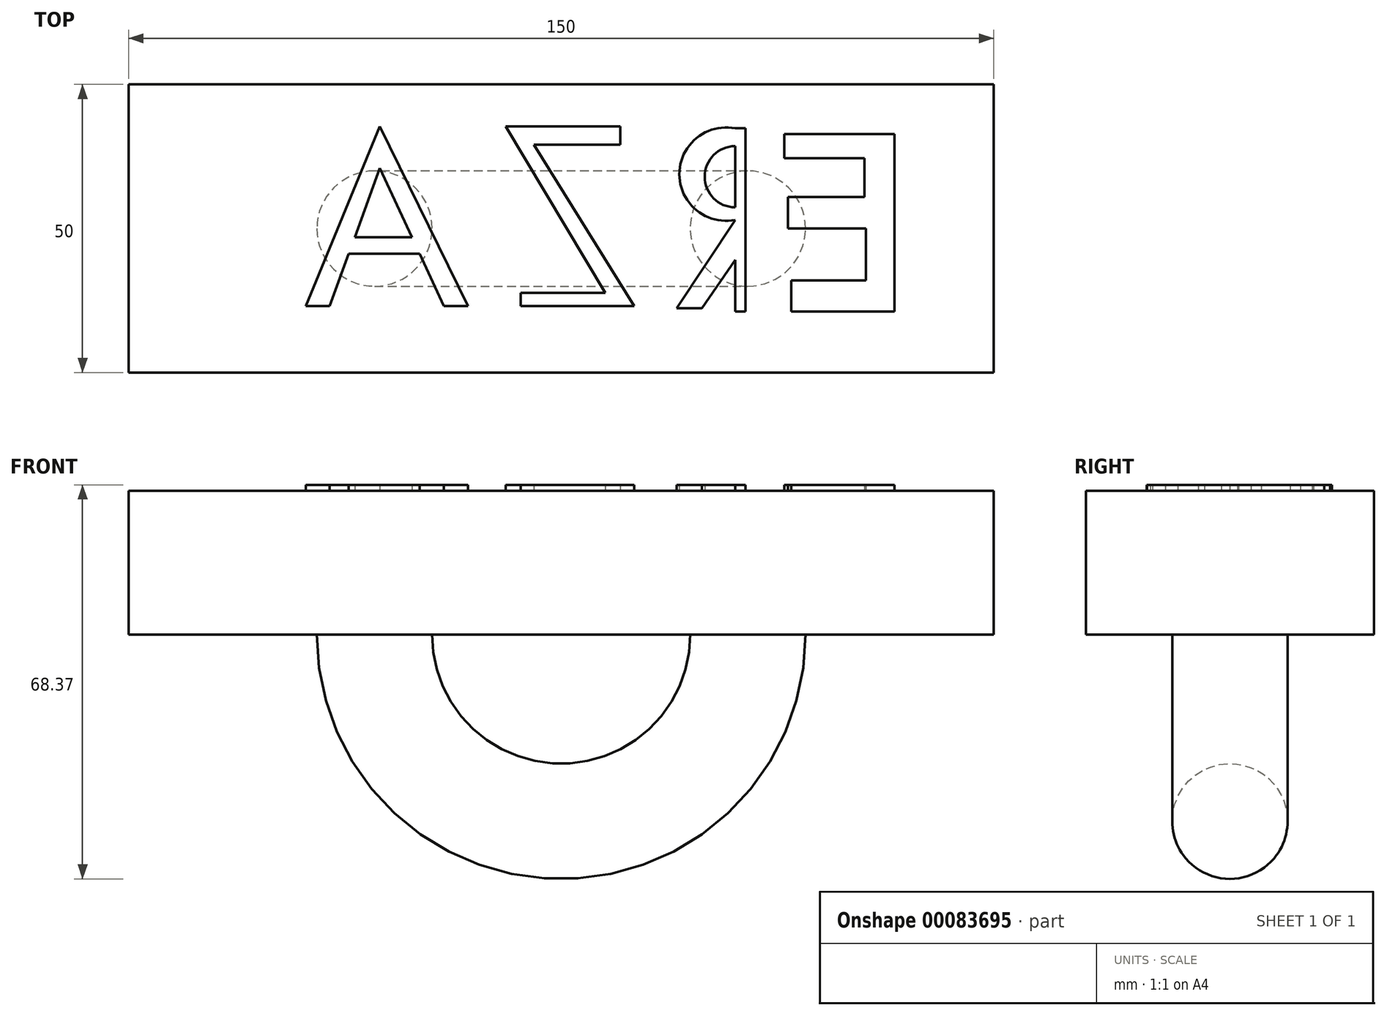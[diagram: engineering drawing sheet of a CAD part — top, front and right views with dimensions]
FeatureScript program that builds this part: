
annotation { "Feature Type Name" : "Feature", "Feature Type Description" : "" }
export const myFeature = defineFeature(function(context is Context, id is Id, definition is map)
    precondition{}
    {
        {
            var Q0;
            Q0=qCreatedBy(makeId("Top.planeOp"),FACE);
            var sketch = newSketch(context, id + "F0", { "sketchPlane" : qUnion([Q0])});
            skLineSegment(sketch, "E0.bottom", {"start": v(-75, 25) * mm, "end": v(75, 25) * mm});
            skLineSegment(sketch, "E0.top", {"start": v(-75, -25) * mm, "end": v(75, -25) * mm});
            skLineSegment(sketch, "E0.left", {"start": v(-75, 25) * mm, "end": v(-75, -25) * mm});
            skLineSegment(sketch, "E0.right", {"start": v(75, 25) * mm, "end": v(75, -25) * mm});
            skPoint(sketch, "E0.middle", {"position": v(0, 0) * mm});
            skSolve(sketch);
        }
        {
            var Q0;
            Q0=makeQuery(id+"F0.imprint","IMPRINT",FACE,{"disambiguationData":[TD([[makeQuery(id+"F0.imprint","IMPRINT",EDGE,{"derivedFrom":sQuery(id+"F0.wireOp",EDGE,"E0.bottom")}),-1.0]])]});
            extrude(context, id + "F1", {"entities" : qUnion([Q0]), "depth" : 25 * mm});
        }
        {
            var Q0;
            Q0=makeQuery(id+"F1.opExtrude","CAP_FACE",FACE,{"disambiguationData":[OSD([sQuery(id+"F0.wireOp",EDGE,"E0.bottom"),sQuery(id+"F0.wireOp",EDGE,"E0.top"),sQuery(id+"F0.wireOp",EDGE,"E0.left"),sQuery(id+"F0.wireOp",EDGE,"E0.right")])],"isStart":false});
            var sketch = newSketch(context, id + "F2", { "sketchPlane" : qUnion([Q0])});
            skLineSegment(sketch, "E1", {"start": v(38.73, 16.39) * mm, "end": v(57.8, 16.39) * mm});
            skLineSegment(sketch, "E2", {"start": v(57.8, 16.39) * mm, "end": v(57.8, -14.4) * mm});
            skLineSegment(sketch, "E3", {"start": v(57.8, -14.4) * mm, "end": v(39.92, -14.4) * mm});
            skLineSegment(sketch, "E4", {"start": v(39.92, -14.4) * mm, "end": v(39.92, -9.04) * mm});
            skLineSegment(sketch, "E5", {"start": v(39.92, -9.04) * mm, "end": v(52.83, -9.04) * mm});
            skLineSegment(sketch, "E6", {"start": v(52.83, -9.04) * mm, "end": v(52.83, 0) * mm});
            skLineSegment(sketch, "E7", {"start": v(52.83, 0) * mm, "end": v(39.33, 0) * mm});
            skLineSegment(sketch, "E8", {"start": v(39.33, 0) * mm, "end": v(39.33, 5.46) * mm});
            skLineSegment(sketch, "E9", {"start": v(39.33, 5.46) * mm, "end": v(52.63, 5.46) * mm});
            skLineSegment(sketch, "E10", {"start": v(52.63, 5.46) * mm, "end": v(52.63, 12.21) * mm});
            skLineSegment(sketch, "E11", {"start": v(52.63, 12.21) * mm, "end": v(38.73, 12.21) * mm});
            skLineSegment(sketch, "E12", {"start": v(38.73, 12.21) * mm, "end": v(38.73, 16.39) * mm});
            skLineSegment(sketch, "E13", {"start": v(30.19, -14.4) * mm, "end": v(30.19, -5.46) * mm});
            skArc(sketch, "E14", {"start": v(30.19, 17.38) * mm, "mid": v(20.5, 9.43) * mm, "end": v(30.19, 1.49) * mm});
            skLineSegment(sketch, "E15", {"start": v(30.19, 1.49) * mm, "end": v(20.06, -13.8) * mm});
            skLineSegment(sketch, "E16", {"start": v(20.06, -13.8) * mm, "end": v(24.43, -13.8) * mm});
            skLineSegment(sketch, "E17", {"start": v(24.43, -13.8) * mm, "end": v(30.19, -5.46) * mm});
            skArc(sketch, "E18", {"start": v(30.19, 14.3) * mm, "mid": v(24.9, 8.99) * mm, "end": v(30.19, 3.67) * mm});
            skPoint(sketch, "E18.startSnap0", {"position": v(38.73, 14.3) * mm});
            skLineSegment(sketch, "E19", {"start": v(30.19, 17.38) * mm, "end": v(31.97, 17.38) * mm});
            skLineSegment(sketch, "E20", {"start": v(31.97, 17.38) * mm, "end": v(31.97, -14.42) * mm});
            skLineSegment(sketch, "E21", {"start": v(31.97, -14.42) * mm, "end": v(30.19, -14.4) * mm});
            skLineSegment(sketch, "E22.trimOffspring", {"start": v(30.19, 3.67) * mm, "end": v(30.19, 14.3) * mm});
            skLineSegment(sketch, "E23", {"start": v(10.24, 17.7) * mm, "end": v(-6.72, 17.7) * mm});
            skLineSegment(sketch, "E24", {"start": v(-4.74, 14.53) * mm, "end": v(12.66, -13.44) * mm});
            skLineSegment(sketch, "E25", {"start": v(12.66, -13.44) * mm, "end": v(-7.05, -13.44) * mm});
            skLineSegment(sketch, "E26", {"start": v(10.24, 17.7) * mm, "end": v(10.24, 14.53) * mm});
            skLineSegment(sketch, "E27", {"start": v(10.24, 14.53) * mm, "end": v(-4.74, 14.53) * mm});
            skLineSegment(sketch, "E28", {"start": v(-7.05, -13.44) * mm, "end": v(-7.05, -11.19) * mm});
            skLineSegment(sketch, "E29", {"start": v(-7.05, -11.19) * mm, "end": v(7.65, -11.19) * mm});
            skLineSegment(sketch, "E30", {"start": v(7.65, -11.19) * mm, "end": v(-9.64, 17.7) * mm});
            skLineSegment(sketch, "E31", {"start": v(-9.64, 17.7) * mm, "end": v(-6.72, 17.7) * mm});
            skLineSegment(sketch, "E32", {"start": v(-16.18, -13.44) * mm, "end": v(-31.46, 17.73) * mm});
            skLineSegment(sketch, "E33", {"start": v(-31.46, 17.73) * mm, "end": v(-44.32, -13.44) * mm});
            skLineSegment(sketch, "E34", {"start": v(-44.32, -13.44) * mm, "end": v(-40.14, -13.44) * mm});
            skLineSegment(sketch, "E35", {"start": v(-40.14, -13.44) * mm, "end": v(-36.85, -4.38) * mm});
            skLineSegment(sketch, "E36", {"start": v(-31.46, 10.46) * mm, "end": v(-25.9, -1.49) * mm});
            skLineSegment(sketch, "E37", {"start": v(-20.35, -13.44) * mm, "end": v(-16.18, -13.44) * mm});
            skLineSegment(sketch, "E38", {"start": v(-25.9, -1.49) * mm, "end": v(-35.8, -1.49) * mm});
            skLineSegment(sketch, "E39", {"start": v(-36.85, -4.38) * mm, "end": v(-24.56, -4.38) * mm});
            skLineSegment(sketch, "E40.trimOffspring", {"start": v(-24.56, -4.38) * mm, "end": v(-20.35, -13.44) * mm});
            skLineSegment(sketch, "E41.trimOffspring", {"start": v(-35.8, -1.49) * mm, "end": v(-31.46, 10.46) * mm});
            skSolve(sketch);
        }
        {
            var Q0;
            Q0=makeQuery(id+"F2.imprint","IMPRINT",FACE,{"disambiguationData":[TD([[makeQuery(id+"F2.imprint","IMPRINT",EDGE,{"derivedFrom":sQuery(id+"F2.wireOp",EDGE,"E32")}),1.0]])]});
            var Q1;
            Q1=makeQuery(id+"F2.imprint","IMPRINT",FACE,{"disambiguationData":[TD([[makeQuery(id+"F2.imprint","IMPRINT",EDGE,{"derivedFrom":sQuery(id+"F2.wireOp",EDGE,"E23")}),1.0]])]});
            var Q2;
            Q2=makeQuery(id+"F2.imprint","IMPRINT",FACE,{"disambiguationData":[TD([[makeQuery(id+"F2.imprint","IMPRINT",EDGE,{"derivedFrom":sQuery(id+"F2.wireOp",EDGE,"E13")}),-1.0]])]});
            var Q3;
            Q3=makeQuery(id+"F2.imprint","IMPRINT",FACE,{"disambiguationData":[TD([[makeQuery(id+"F2.imprint","IMPRINT",EDGE,{"derivedFrom":sQuery(id+"F2.wireOp",EDGE,"E1")}),-1.0]])]});
            extrude(context, id + "F3", {"entities" : qUnion([Q0, Q1, Q2, Q3]), "operationType" : NewBodyOperationType.ADD, "depth" : 1 * mm});
        }
        {
            var Q0;
            Q0=makeQuery(id+"F1.opExtrude","CAP_FACE",FACE,{"disambiguationData":[OSD([sQuery(id+"F0.wireOp",EDGE,"E0.bottom"),sQuery(id+"F0.wireOp",EDGE,"E0.top"),sQuery(id+"F0.wireOp",EDGE,"E0.left"),sQuery(id+"F0.wireOp",EDGE,"E0.right")])],"isStart":true});
            var sketch = newSketch(context, id + "F4", { "sketchPlane" : qUnion([Q0])});
            skCircle(sketch, "E42", {"center": v(32.37, 0) * mm, "radius": 10 * mm});
            skLineSegment(sketch, "E43", {"start": v(0, -18.57) * mm, "end": v(0, 18.97) * mm, "construction": true});
            skSolve(sketch);
        }
        {
            var Q0;
            Q0=makeQuery(id+"F4.imprint","IMPRINT",FACE,{"disambiguationData":[TD([[makeQuery(id+"F4.imprint","IMPRINT",EDGE,{"derivedFrom":sQuery(id+"F4.wireOp",EDGE,"E42")}),1.0]])]});
            var Q1;
            Q1=sQuery(id+"F4.wireOp",EDGE,"E43");
            revolve(context, id + "F5", {"operationType" : NewBodyOperationType.ADD, "entities" : qUnion([Q0]), "axis" : qUnion([Q1]), "revolveType" : RevolveType.ONE_DIRECTION, "oppositeDirection" : true, "angle" : 180 * degree});
        }
    });
